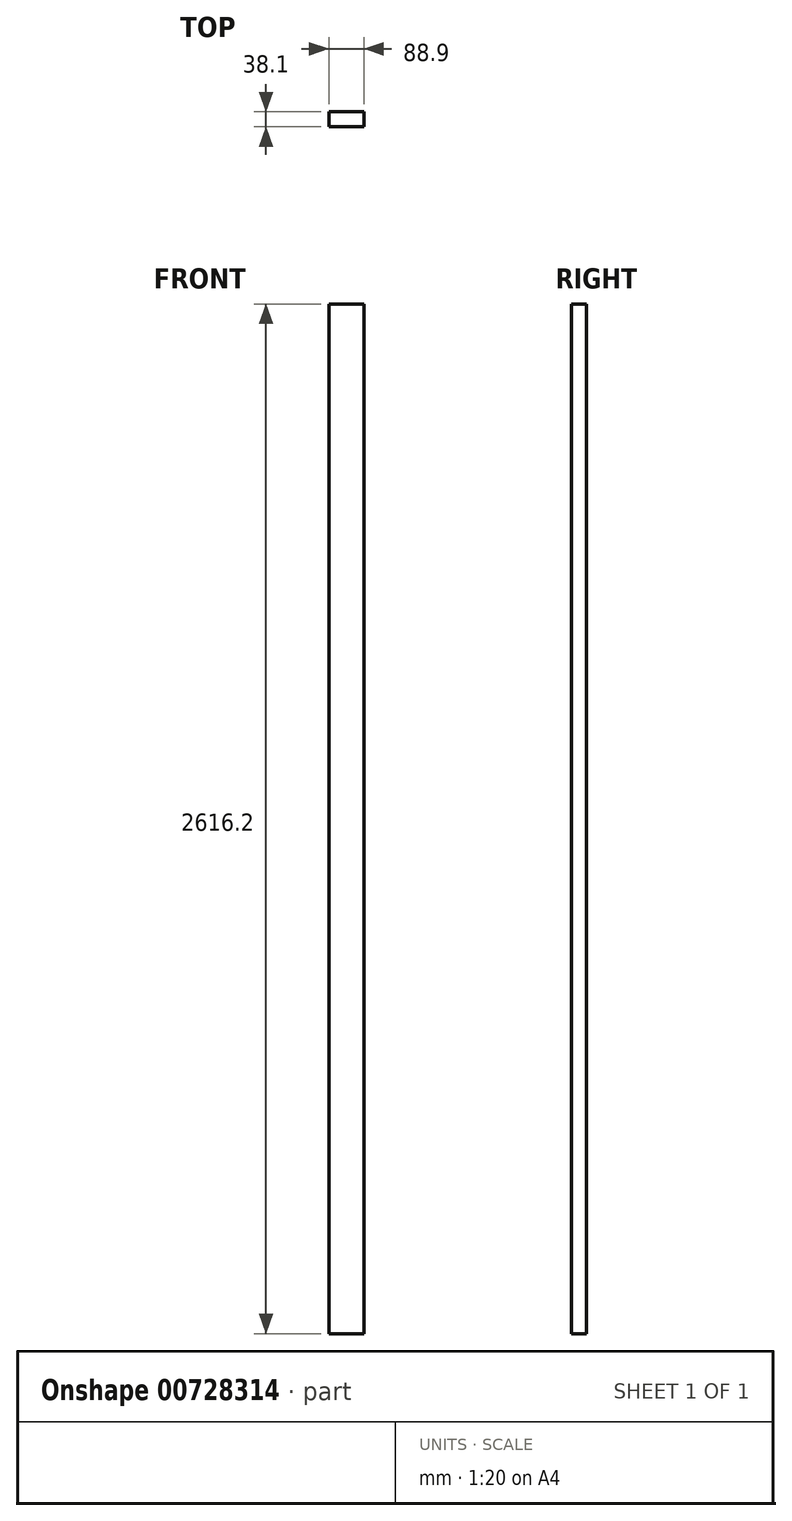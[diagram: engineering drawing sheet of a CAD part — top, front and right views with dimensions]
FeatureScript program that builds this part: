
annotation { "Feature Type Name" : "Feature", "Feature Type Description" : "" }
export const myFeature = defineFeature(function(context is Context, id is Id, definition is map)
    precondition{}
    {
        {
            var Q0;
            Q0=qCreatedBy(makeId("Front.planeOp"),FACE);
            var sketch = newSketch(context, id + "F0", { "sketchPlane" : qUnion([Q0])});
            skLineSegment(sketch, "E0.bottom", {"start": v(-44.45, -1308.1) * mm, "end": v(44.45, -1308.1) * mm});
            skLineSegment(sketch, "E0.top", {"start": v(-44.45, 1308.1) * mm, "end": v(44.45, 1308.1) * mm});
            skLineSegment(sketch, "E0.left", {"start": v(-44.45, -1308.1) * mm, "end": v(-44.45, 1308.1) * mm});
            skLineSegment(sketch, "E0.right", {"start": v(44.45, -1308.1) * mm, "end": v(44.45, 1308.1) * mm});
            skPoint(sketch, "E0.middle", {"position": v(0, 0) * mm});
            skSolve(sketch);
        }
        {
            var Q0;
            Q0=qSketchRegion(id+"F0",true);
            extrude(context, id + "F1", {"entities" : qUnion([Q0]), "depth" : 38.1 * mm});
        }
    });
